# Revit family: Faucet-Pull_Down-American_Standard-Hillsdale-7617300_Series
name_source: partatom
category: Plumbing Fixtures
revit_build: Autodesk Revit 2018 (Build: 20170223_1515(x64)
units: mm (PartAtom-declared; Revit-internal decimal feet)

## family parameters
Always vertical = No
Cut with Voids When Loaded = No
OmniClass Number = 23.45.55.14
OmniClass Title = Single Faucets
Part Type = Normal
Room Calculation Point = No
Round Connector Dimension = Use Diameter
Shared = Yes
Work Plane-Based = Yes

## types (3) — shared parameters
ADA Compliant = Yes
Assembly Code = D2020300
CW Connection = No
CWFU = 1.5
Compliance Certifications = Product meet or exceeds ANSI A117.1, ASME A112.18.1, CSA B125.1, NSF 61/Section 9,NSF 372
Deck Plate Height = 1/4"
Deck-Plate = Yes
Deckplate Width = 10 11/16"
Default Elevation = 0"
Description = Hillsdale™ Single-Handle Pull-Down Dual Spray Kitchen Faucet
Flow Rate = 1.8 gpm (6.8 L/min.)
HW Connection = No
HWFU = 1.5
Height = 16 7/16"
Installation Type = Deck Mounted
Manufacturer = American Standard
Price = Prices may vary. Please consult Manufacturer Representative for most up-to-date price list.
Product Documentation Link = https://americanstandard.box.com
Product Page URL = https://www.americanstandard-us.com
Tempered Connection = Yes
Tempered Water Connection Diameter = 3/8"
Tempered Water Connection Radius = 3/16"
URL = https://www.americanstandard-us.com
Vent Connection = No
WFU = 2
Waste Connection = No
Width = 10 9/16"

## per-type parameters (varying)
| type | Finish | Material |
| 7617300.002 | Metal-American Standard-002-Polished Chrome | Metal-American Standard-002-Polished Chrome |
| 7617300.243 | Metal-American Standard-243-Matte Black | Metal-American Standard-243-Matte Black |
| 7617300.075 | Metal-American Standard-075-Stainless Steel | Metal-American Standard-075-Stainless Steel |

note: column(s) folded — value = type name in every type: Model

## geometry (parser evidence)
native form markers: Sweep x5
no freeform markers — native parametric forms only
